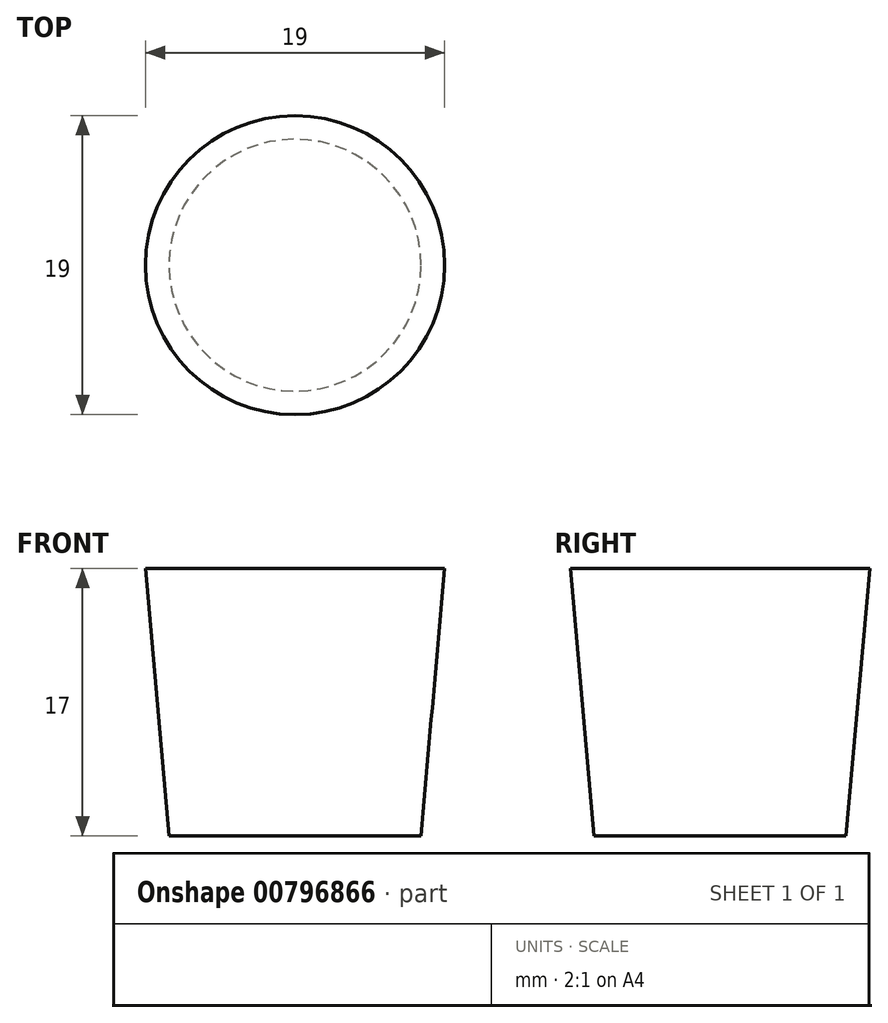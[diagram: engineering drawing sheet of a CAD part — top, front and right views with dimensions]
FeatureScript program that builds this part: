
annotation { "Feature Type Name" : "Feature", "Feature Type Description" : "" }
export const myFeature = defineFeature(function(context is Context, id is Id, definition is map)
    precondition{}
    {
        {
            var Q0;
            Q0=qCreatedBy(makeId("Front.planeOp"),FACE);
            var sketch = newSketch(context, id + "F0", { "sketchPlane" : qUnion([Q0])});
            skLineSegment(sketch, "E0", {"start": v(0, 0) * mm, "end": v(-9.5, 0) * mm});
            skLineSegment(sketch, "E1", {"start": v(0, 0) * mm, "end": v(0, -17) * mm});
            skLineSegment(sketch, "E2", {"start": v(0, -17) * mm, "end": v(-8, -17) * mm});
            skLineSegment(sketch, "E3", {"start": v(-8, -17) * mm, "end": v(-9.5, 0) * mm});
            skSolve(sketch);
        }
        {
            var Q0;
            Q0=makeQuery(id+"F0.imprint","IMPRINT",FACE,{"disambiguationData":[TD([[makeQuery(id+"F0.imprint","IMPRINT",EDGE,{"derivedFrom":sQuery(id+"F0.wireOp",EDGE,"E0")}),1.0]])]});
            var Q1;
            Q1=sQuery(id+"F0.wireOp",EDGE,"E1");
            revolve(context, id + "F1", {"surfaceOperationType" : NewSurfaceOperationType.NEW, "entities" : qUnion([Q0]), "axis" : qUnion([Q1]), "revolveType" : RevolveType.FULL});
        }
        {
            var Q0;
            Q0=makeQuery(id+"F1.opRevolve","SWEPT_BODY",BODY,{"disambiguationData":[OSD([sQuery(id+"F0.wireOp",EDGE,"E0"),sQuery(id+"F0.wireOp",EDGE,"E1"),sQuery(id+"F0.wireOp",EDGE,"E2"),sQuery(id+"F0.wireOp",EDGE,"E3")])]});
            transform(context, id + "F2", {"entities" : qUnion([Q0]), "transformType" : TransformType.TRANSLATION_3D, "dx" : 0 * mm, "dy" : 0 * mm, "dz" : 0 * mm, "makeCopy" : true});
        }
    });
